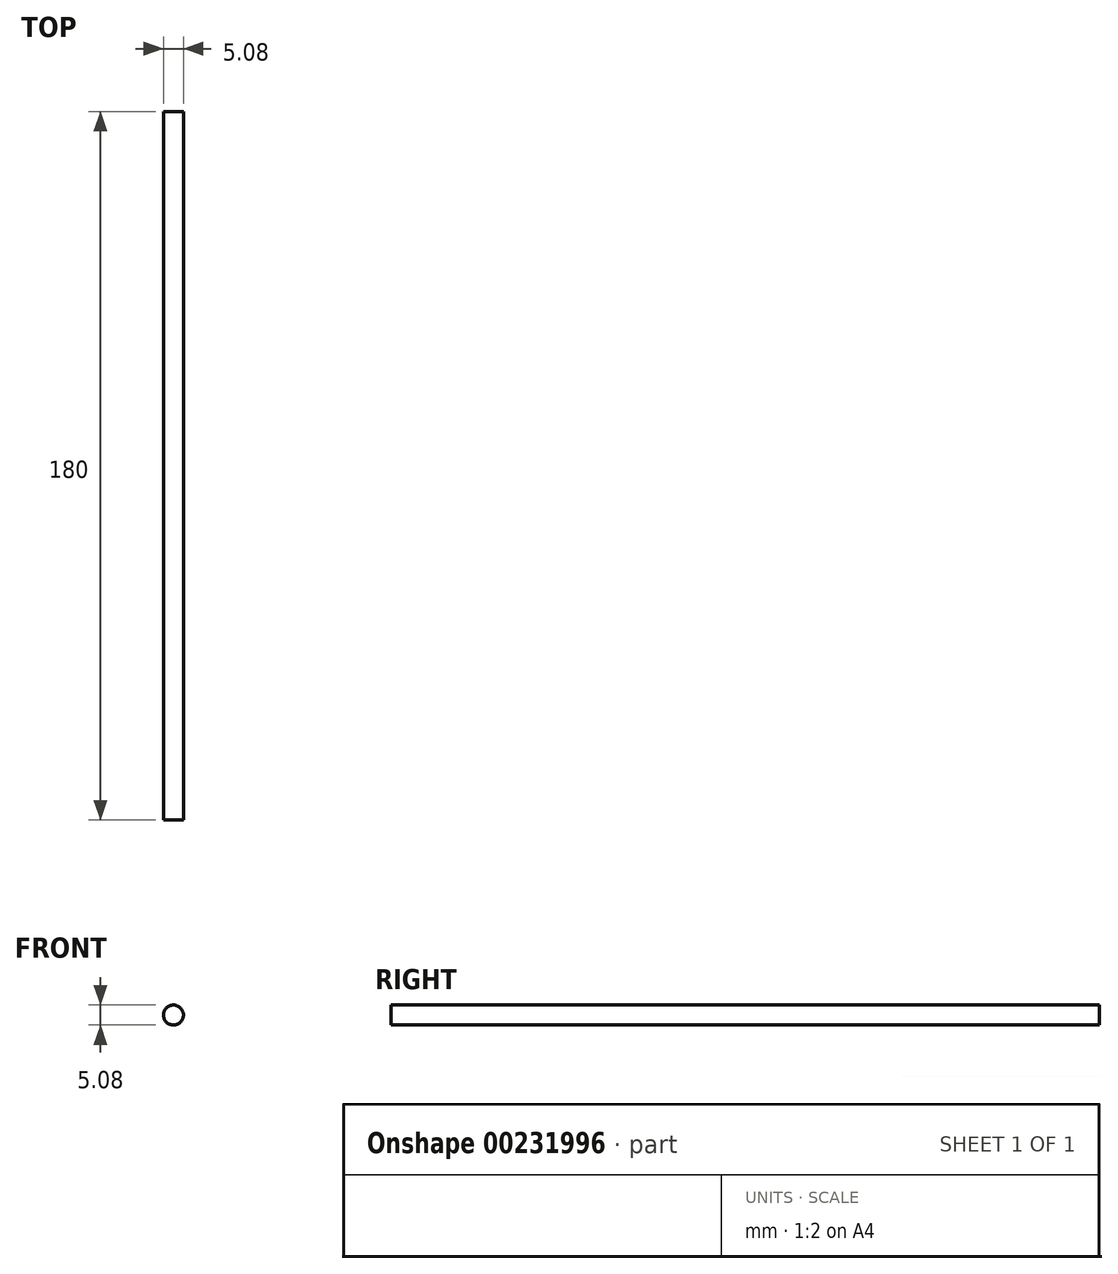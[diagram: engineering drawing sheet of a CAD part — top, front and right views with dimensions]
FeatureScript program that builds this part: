
annotation { "Feature Type Name" : "Feature", "Feature Type Description" : "" }
export const myFeature = defineFeature(function(context is Context, id is Id, definition is map)
    precondition{}
    {
        {
            var Q0;
            Q0=qCreatedBy(makeId("Front.planeOp"),FACE);
            var sketch = newSketch(context, id + "F0", { "sketchPlane" : qUnion([Q0])});
            skCircle(sketch, "E0", {"center": v(0, 0) * mm, "radius": 2.54 * mm});
            skSolve(sketch);
        }
        {
            var Q0;
            Q0 = qSketchRegion(id + "F0", true);
            extrude(context, id + "F1", {"entities" : qUnion([Q0]), "depth" : 180 * mm});
        }
    });
